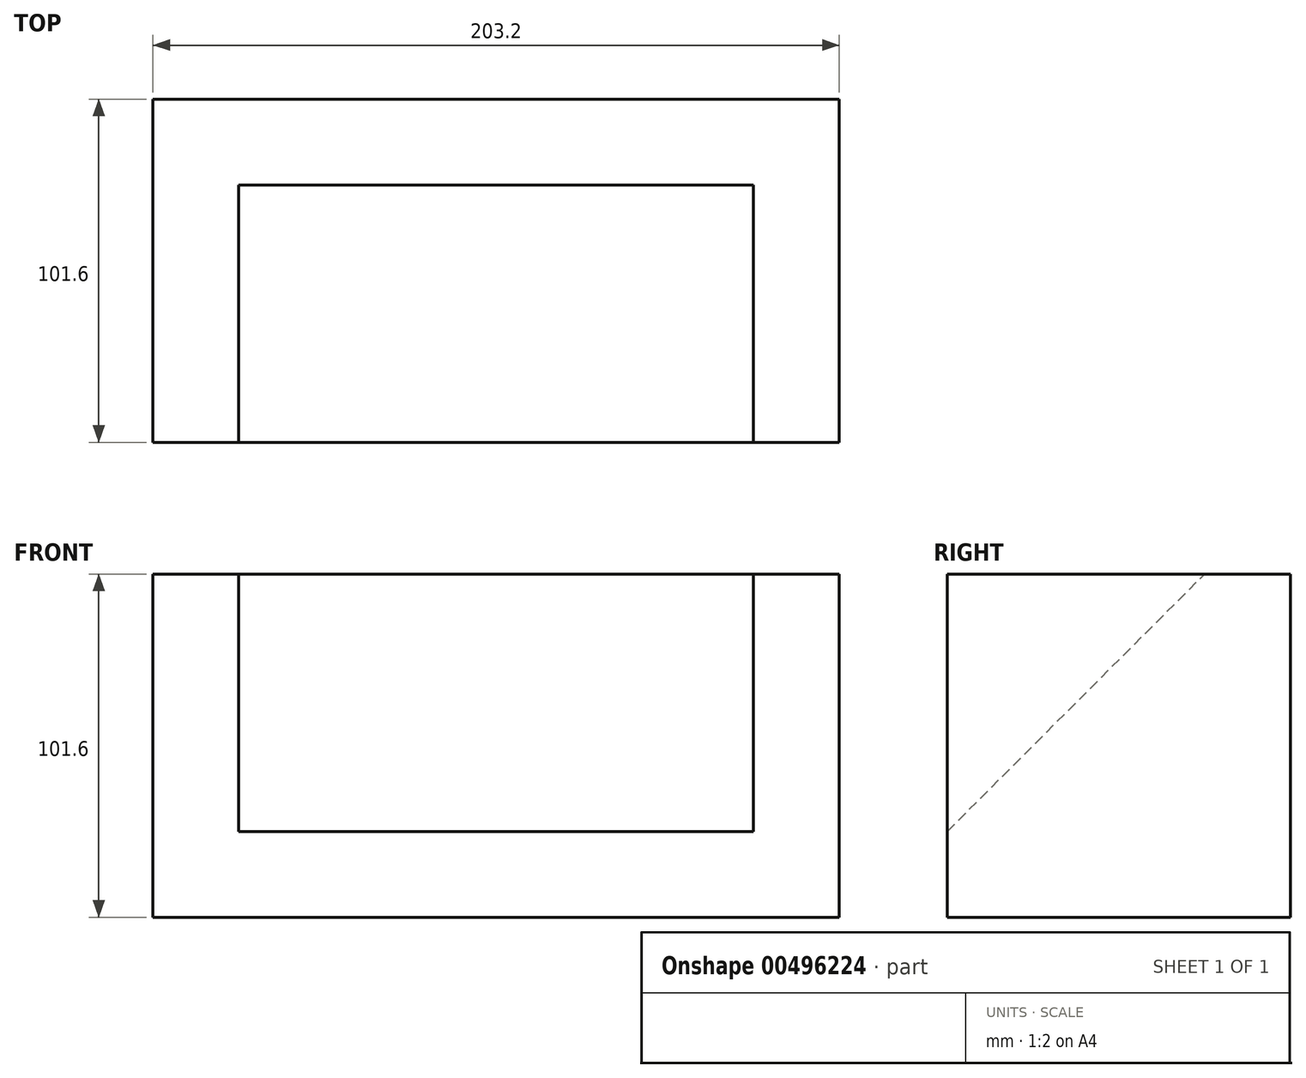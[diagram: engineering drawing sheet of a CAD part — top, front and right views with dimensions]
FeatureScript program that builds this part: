
annotation { "Feature Type Name" : "Feature", "Feature Type Description" : "" }
export const myFeature = defineFeature(function(context is Context, id is Id, definition is map)
    precondition{}
    {
        {
            var Q0;
            Q0=qCreatedBy(makeId("Top.planeOp"),FACE);
            var sketch = newSketch(context, id + "F0", { "sketchPlane" : qUnion([Q0])});
            skLineSegment(sketch, "E0.bottom", {"start": v(-75.65, 0) * mm, "end": v(127.55, 0) * mm});
            skLineSegment(sketch, "E0.top", {"start": v(-75.65, -101.6) * mm, "end": v(127.55, -101.6) * mm});
            skLineSegment(sketch, "E0.left", {"start": v(-75.65, 0) * mm, "end": v(-75.65, -101.6) * mm});
            skLineSegment(sketch, "E0.right", {"start": v(127.55, 0) * mm, "end": v(127.55, -101.6) * mm});
            skSolve(sketch);
        }
        {
            var Q0;
            Q0 = qSketchRegion(id + "F0", true);
            extrude(context, id + "F1", {"entities" : qUnion([Q0]), "depth" : 25.4 * mm});
        }
        {
            var Q0;
            Q0=makeQuery(id+"F1.opExtrude","CAP_FACE",FACE,{"disambiguationData":[OSD([sQuery(id+"F0.wireOp",EDGE,"E0.bottom"),sQuery(id+"F0.wireOp",EDGE,"E0.top"),sQuery(id+"F0.wireOp",EDGE,"E0.left"),sQuery(id+"F0.wireOp",EDGE,"E0.right")])],"isStart":false});
            var sketch = newSketch(context, id + "F2", { "sketchPlane" : qUnion([Q0])});
            skLineSegment(sketch, "E1.bottom", {"start": v(-50.25, -101.6) * mm, "end": v(102.15, -101.6) * mm});
            skLineSegment(sketch, "E1.top", {"start": v(-50.25, -25.4) * mm, "end": v(102.15, -25.4) * mm});
            skLineSegment(sketch, "E1.left", {"start": v(-50.25, -101.6) * mm, "end": v(-50.25, -25.4) * mm});
            skLineSegment(sketch, "E1.right", {"start": v(102.15, -101.6) * mm, "end": v(102.15, -25.4) * mm});
            skSolve(sketch);
        }
        {
            var Q0;
            Q0 = qSketchRegion(id + "F2", true);
            extrude(context, id + "F3", {"entities" : qUnion([Q0]), "operationType" : NewBodyOperationType.ADD, "depth" : 76.2 * mm});
        }
        {
            var Q0;
            Q0=makeQuery(id+"F3.opExtrude","SWEPT_FACE",FACE,{"disambiguationData":[OSD([sQuery(id+"F2.wireOp",EDGE,"E1.right")])]});
            var sketch = newSketch(context, id + "F4", { "sketchPlane" : qUnion([Q0])});
            skLineSegment(sketch, "E2", {"start": v(-101.6, 25.4) * mm, "end": v(-25.4, 101.6) * mm});
            skLineSegment(sketch, "E3", {"start": v(-25.4, 101.6) * mm, "end": v(-101.6, 101.6) * mm});
            skLineSegment(sketch, "E4", {"start": v(-101.6, 101.6) * mm, "end": v(-101.6, 25.4) * mm});
            skSolve(sketch);
        }
        {
            var Q0;
            Q0=makeQuery(id+"F4.imprint","IMPRINT",FACE,{"disambiguationData":[TD([[makeQuery(id+"F4.imprint","IMPRINT",EDGE,{"derivedFrom":sQuery(id+"F4.wireOp",EDGE,"E2")}),1.0]])]});
            extrude(context, id + "F5", {"entities" : qUnion([Q0]), "operationType" : NewBodyOperationType.REMOVE, "endBound" : BoundingType.UP_TO_NEXT, "oppositeDirection" : true, "depth" : mm});
        }
        {
            var Q0;
            Q0=makeQuery(id+"F1.opExtrude","CAP_FACE",FACE,{"disambiguationData":[OSD([sQuery(id+"F0.wireOp",EDGE,"E0.bottom"),sQuery(id+"F0.wireOp",EDGE,"E0.top"),sQuery(id+"F0.wireOp",EDGE,"E0.left"),sQuery(id+"F0.wireOp",EDGE,"E0.right")])],"isStart":false});
            var sketch = newSketch(context, id + "F6", { "sketchPlane" : qUnion([Q0])});
            skLineSegment(sketch, "E5", {"start": v(-75.65, -101.6) * mm, "end": v(-50.25, -101.6) * mm});
            skLineSegment(sketch, "E6", {"start": v(-50.25, -101.6) * mm, "end": v(-50.25, -25.4) * mm});
            skLineSegment(sketch, "E7", {"start": v(-50.25, -25.4) * mm, "end": v(102.15, -25.4) * mm});
            skLineSegment(sketch, "E8", {"start": v(102.15, -25.4) * mm, "end": v(102.15, -101.6) * mm});
            skLineSegment(sketch, "E9", {"start": v(102.15, -101.6) * mm, "end": v(127.55, -101.6) * mm});
            skLineSegment(sketch, "E10", {"start": v(127.55, -101.6) * mm, "end": v(127.55, 0) * mm});
            skLineSegment(sketch, "E11", {"start": v(127.55, 0) * mm, "end": v(-75.65, 0) * mm});
            skLineSegment(sketch, "E12", {"start": v(-75.65, 0) * mm, "end": v(-75.65, -101.6) * mm});
            skSolve(sketch);
        }
        {
            var Q0;
            Q0 = qSketchRegion(id + "F6", true);
            extrude(context, id + "F7", {"entities" : qUnion([Q0]), "operationType" : NewBodyOperationType.ADD, "depth" : 76.2 * mm});
        }
    });
